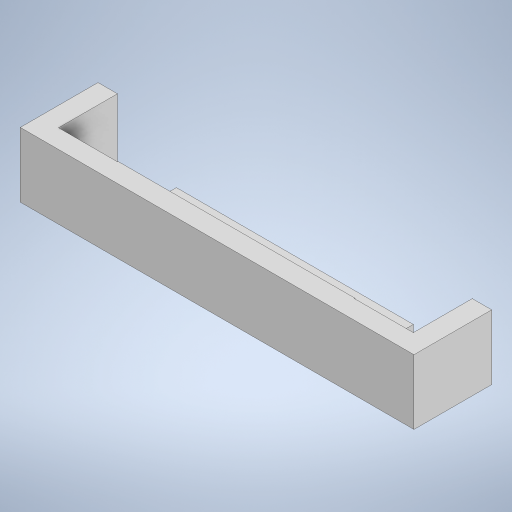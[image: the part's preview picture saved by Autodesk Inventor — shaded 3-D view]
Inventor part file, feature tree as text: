
AUTODESK INVENTOR PART (.ipt)
format: ipt  version: 2024 (Build 280153000, 153)  size: 268,800 bytes
history: native  units: mm
features: extrude x5, sketch x5, projected_geometry x2
ambient origin geometry x8: Origin, YZ Plane, XZ Plane, XY Plane, X Axis, Y Axis, Z Axis, Center Point
bodies: Solid1 (feature_tree)
feature tree (12):
  extrude  "Extrusion1"  Depth=60.0mm
  extrude  "Extrusion2"  Depth=15.0mm
  extrude  "Extrusion3"  Depth=45.5mm
  extrude  "Extrusion4"  Depth=45.5mm TaperAngle=0.0deg
  extrude  "Extrusion5"  Depth=60.0mm
  sketch  "Sketch1"  dims[d0=274.0mm d1=60.0mm]
  sketch  "Sketch2"  dims[d2=10.0mm d3=0.0mm d4=15.0mm]
  projected_geometry  "Projected Loop1"
  sketch  "Sketch3"  dims[d5=50.0mm d6=0.0mm d7=45.5mm]
  sketch  "Sketch4"  dims[d8=45.5mm d9=150.0mm d10=0.0mm]
  projected_geometry  "Projected Loop2"
  sketch  "Sketch5"  dims[d11=60.0mm d12=60.0mm d13=15.0mm d14=15.0mm d15=50.0mm d16=0.0mm d17=0.0mm d18=0.0mm]
